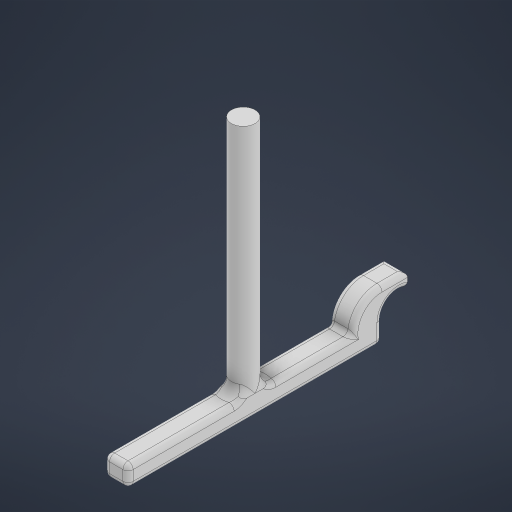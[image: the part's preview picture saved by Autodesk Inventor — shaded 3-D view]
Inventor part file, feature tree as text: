
AUTODESK INVENTOR PART (.ipt)
format: ipt  version: 2024.1 (Build 281209000, 209)  size: 741,376 bytes
history: native  units: mm
features: extrude x3, fillet x3, sketch x3
ambient origin geometry x8: Origin, YZ Plane, XZ Plane, XY Plane, X Axis, Y Axis, Z Axis, Center Point
bodies: Solid1 (feature_tree)
feature tree (9):
  extrude  "Extrusion1"  Depth=50.0mm TaperAngle=0.0deg
  extrude  "Extrusion2"  Depth=4.0mm TaperAngle=0.0deg
  extrude  "Extrusion3"  Depth=2.0mm
  fillet  "Fillet3"  Radius=1.0mm
  fillet  "Fillet4"  Radius=1.0mm
  fillet  "Fillet5"  [1 undecoded]
  sketch  "Sketch1"  dims[d0=4.64mm d1=50.0mm d2=0.0mm]
  sketch  "Sketch2"  dims[d4=50.0mm d5=4.0mm d6=0.0mm]
  sketch  "Sketch3"  dims[d7=10.0mm d8=0.0mm d11=2.0mm d12=1.0mm d13=1.0mm d10=0.0mm]
note: 1 required parameter value undecoded (feature->parameter linkage not recoverable at this tier; creation-order binding heuristic only, values carry confidence <= 0.55)
